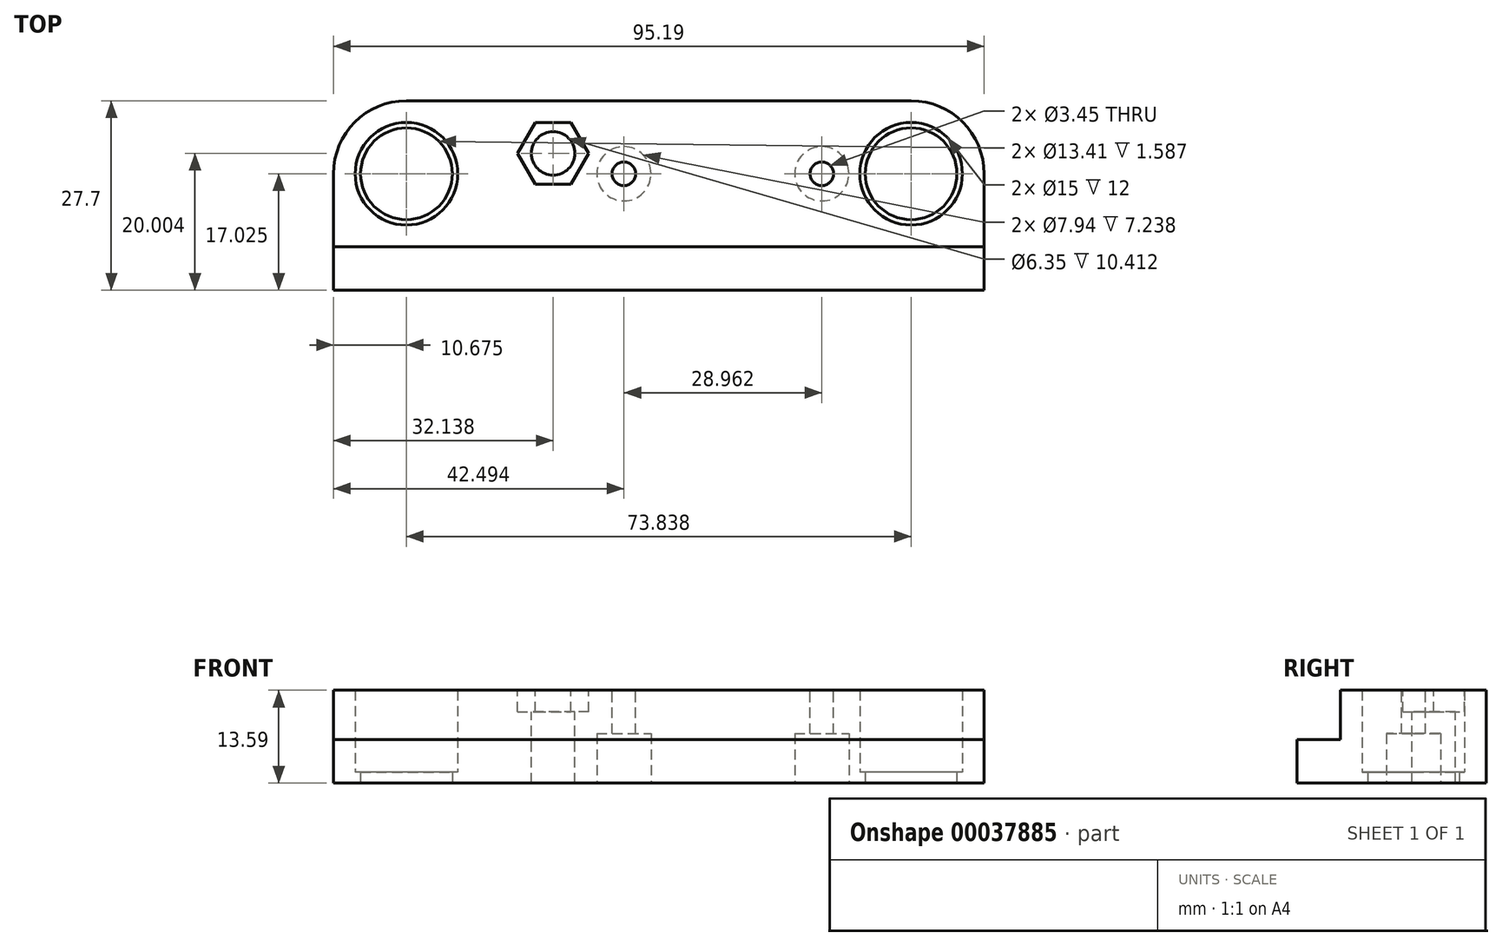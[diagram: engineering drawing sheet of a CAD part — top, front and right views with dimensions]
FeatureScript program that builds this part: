
annotation { "Feature Type Name" : "Feature", "Feature Type Description" : "" }
export const myFeature = defineFeature(function(context is Context, id is Id, definition is map)
    precondition{}
    {
        {
            var Q0;
            Q0=qCreatedBy(makeId("Top.planeOp"),FACE);
            var sketch = newSketch(context, id + "F0", { "sketchPlane" : qUnion([Q0])});
            skLineSegment(sketch, "E0.bottom", {"start": v(0, 0) * mm, "end": v(95.19, 0) * mm});
            skLineSegment(sketch, "E0.top", {"start": v(0, -27.7) * mm, "end": v(95.19, -27.7) * mm});
            skLineSegment(sketch, "E0.left", {"start": v(0, 0) * mm, "end": v(0, -27.7) * mm});
            skLineSegment(sketch, "E0.right", {"start": v(95.19, 0) * mm, "end": v(95.19, -27.7) * mm});
            skLineSegment(sketch, "E1", {"start": v(10.67, 0) * mm, "end": v(10.67, -10.67) * mm, "construction": true});
            skLineSegment(sketch, "E2", {"start": v(10.67, -10.67) * mm, "end": v(0, -10.67) * mm, "construction": true});
            skLineSegment(sketch, "E3", {"start": v(95.19, -10.67) * mm, "end": v(84.51, -10.67) * mm, "construction": true});
            skCircle(sketch, "E4", {"center": v(10.67, -10.67) * mm, "radius": 6.7 * mm});
            skCircle(sketch, "E5", {"center": v(84.51, -10.67) * mm, "radius": 6.7 * mm});
            skSolve(sketch);
        }
        {
            var Q0;
            Q0=qSketchRegion(id+"F0",true);
            extrude(context, id + "F1", {"entities" : qUnion([Q0]), "depth" : 1.59 * mm});
        }
        {
            var Q0;
            Q0=makeQuery(id+"F1.opExtrude","SWEPT_EDGE",EDGE,{"disambiguationData":[OSD([sQuery(id+"F0.wireOp",EDGE,"E0.bottom"),sQuery(id+"F0.wireOp",EDGE,"E0.left")])]});
            var Q1;
            Q1=makeQuery(id+"F1.opExtrude","SWEPT_EDGE",EDGE,{"disambiguationData":[OSD([sQuery(id+"F0.wireOp",EDGE,"E0.bottom"),sQuery(id+"F0.wireOp",EDGE,"E0.right")])]});
            fillet(context, id + "F2", {"entities" : qUnion([Q0, Q1]), "radius" : 10.67 * mm, "tangentPropagation" : true, "allowEdgeOverflow" : false});
        }
        {
            var Q0;
            Q0=makeQuery(id+"F1.opExtrude","CAP_FACE",FACE,{"disambiguationData":[OSD([sQuery(id+"F0.wireOp",EDGE,"E0.bottom"),sQuery(id+"F0.wireOp",EDGE,"E0.top"),sQuery(id+"F0.wireOp",EDGE,"E0.left"),sQuery(id+"F0.wireOp",EDGE,"E0.right"),sQuery(id+"F0.wireOp",EDGE,"E4"),sQuery(id+"F0.wireOp",EDGE,"E5")])],"isStart":false});
            var sketch = newSketch(context, id + "F3", { "sketchPlane" : qUnion([Q0])});
            skLineSegment(sketch, "E6.bottom", {"start": v(0, -10.67) * mm, "end": v(95.19, -10.67) * mm, "construction": true});
            skLineSegment(sketch, "E6.top", {"start": v(0, -21.35) * mm, "end": v(95.19, -21.35) * mm});
            skLineSegment(sketch, "E6.left", {"start": v(0, -10.67) * mm, "end": v(0, -21.35) * mm});
            skLineSegment(sketch, "E6.right", {"start": v(95.19, -10.67) * mm, "end": v(95.19, -21.35) * mm});
            skLineSegment(sketch, "E7", {"start": v(47.6, -21.35) * mm, "end": v(47.6, -27.7) * mm, "construction": true});
            skPoint(sketch, "E7.endSnap0", {"position": v(47.6, -27.7) * mm});
            skCircle(sketch, "E8", {"center": v(10.67, -10.67) * mm, "radius": 7.5 * mm});
            skCircle(sketch, "E9", {"center": v(84.51, -10.67) * mm, "radius": 7.5 * mm});
            skSolve(sketch);
        }
        {
            var Q0;
            Q0=makeQuery(id+"F3.imprint","IMPRINT",FACE,{"disambiguationData":[TD([[makeQuery(id+"F3.imprint","IMPRINT",EDGE,{"derivedFrom":sQuery(id+"F3.wireOp",EDGE,"E6.top")}),1.0]])]});
            extrude(context, id + "F4", {"entities" : qUnion([Q0]), "operationType" : NewBodyOperationType.ADD, "depth" : 12 * mm});
        }
        {
            var Q0;
            {var subQ0=sQuery(id+"F0.wireOp",EDGE,"E0.top");var subQ1=sQuery(id+"F0.wireOp",EDGE,"E0.left");var subQ2=sQuery(id+"F0.wireOp",EDGE,"E0.right");Q0=makeQuery(id+"F4.boolean.opBoolean","SPLIT",FACE,{"disambiguationData":[TD([makeQuery(id+"F1.opExtrude","SWEPT_FACE",FACE,{"disambiguationData":[OSD([subQ0])]})])],"derivedFrom":makeQuery(id+"F1.opExtrude","CAP_FACE",FACE,{"disambiguationData":[OSD([sQuery(id+"F0.wireOp",EDGE,"E0.bottom"),subQ0,subQ1,subQ2,sQuery(id+"F0.wireOp",EDGE,"E4"),sQuery(id+"F0.wireOp",EDGE,"E5")])],"isStart":false})});}
            extrude(context, id + "F5", {"entities" : qUnion([Q0]), "operationType" : NewBodyOperationType.ADD, "depth" : 4.76 * mm});
        }
        {
            var Q0;
            Q0=makeQuery(id+"F4.opExtrude","CAP_FACE",FACE,{"disambiguationData":[OSD([sQuery(id+"F0.wireOp",EDGE,"E0.bottom"),sQuery(id+"F0.wireOp",EDGE,"E0.top"),sQuery(id+"F0.wireOp",EDGE,"E0.left"),sQuery(id+"F0.wireOp",EDGE,"E0.right"),sQuery(id+"F0.wireOp",EDGE,"E4"),sQuery(id+"F0.wireOp",EDGE,"E5"),sQuery(id+"F3.wireOp",EDGE,"E6.top"),sQuery(id+"F3.wireOp",EDGE,"E6.left"),sQuery(id+"F3.wireOp",EDGE,"E6.right"),sQuery(id+"F3.wireOp",EDGE,"E8"),sQuery(id+"F3.wireOp",EDGE,"E9")])],"isStart":false});
            var sketch = newSketch(context, id + "F6", { "sketchPlane" : qUnion([Q0])});
            skCircle(sketch, "E10", {"center": v(42.5, -10.67) * mm, "radius": 5.56 * mm, "construction": true});
            skPoint(sketch, "E11", {"position": v(47.6, -10.67) * mm});
            skCircle(sketch, "E12", {"center": v(42.5, -10.67) * mm, "radius": 1.73 * mm});
            skCircle(sketch, "E13", {"center": v(71.46, -10.67) * mm, "radius": 1.73 * mm});
            skLineSegment(sketch, "E14", {"start": v(47.6, -10.67) * mm, "end": v(47.6, -21.35) * mm, "construction": true});
            skCircle(sketch, "E15", {"center": v(32.14, -7.7) * mm, "radius": 3.18 * mm});
            skLineSegment(sketch, "E16", {"start": v(10.67, -10.67) * mm, "end": v(10.67, -7.7) * mm, "construction": true});
            skLineSegment(sketch, "E17", {"start": v(10.67, -7.7) * mm, "end": v(32.14, -7.7) * mm, "construction": true});
            skLineSegment(sketch, "E18", {"start": v(47.6, -10.67) * mm, "end": v(71.46, -10.67) * mm, "construction": true});
            skLineSegment(sketch, "E19", {"start": v(47.6, -10.67) * mm, "end": v(42.5, -10.67) * mm, "construction": true});
            skCircle(sketch, "E20", {"center": v(32.14, -7.7) * mm, "radius": 5.22 * mm, "construction": true});
            skCircle(sketch, "E21", {"center": v(71.46, -10.67) * mm, "radius": 5.56 * mm, "construction": true});
            skSolve(sketch);
        }
        {
            var Q0;
            Q0=qSketchRegion(id+"F6",true);
            var Q1;
            Q1=makeQuery(id+"F1.opExtrude","CAP_FACE",FACE,{"disambiguationData":[OSD([sQuery(id+"F0.wireOp",EDGE,"E0.bottom"),sQuery(id+"F0.wireOp",EDGE,"E0.top"),sQuery(id+"F0.wireOp",EDGE,"E0.left"),sQuery(id+"F0.wireOp",EDGE,"E0.right"),sQuery(id+"F0.wireOp",EDGE,"E4"),sQuery(id+"F0.wireOp",EDGE,"E5")])],"isStart":true});
            extrude(context, id + "F7", {"entities" : qUnion([Q0]), "operationType" : NewBodyOperationType.REMOVE, "endBound" : BoundingType.UP_TO_SURFACE, "oppositeDirection" : true, "endBoundEntityFace" : qUnion([Q1]), "depth" : 25.4 * mm});
        }
        {
            var Q0;
            Q0=makeQuery(id+"F1.opExtrude","CAP_FACE",FACE,{"disambiguationData":[OSD([sQuery(id+"F0.wireOp",EDGE,"E0.bottom"),sQuery(id+"F0.wireOp",EDGE,"E0.top"),sQuery(id+"F0.wireOp",EDGE,"E0.left"),sQuery(id+"F0.wireOp",EDGE,"E0.right"),sQuery(id+"F0.wireOp",EDGE,"E4"),sQuery(id+"F0.wireOp",EDGE,"E5")])],"isStart":true});
            var sketch = newSketch(context, id + "F8", { "sketchPlane" : qUnion([Q0])});
            skCircle(sketch, "E22", {"center": v(71.46, 10.67) * mm, "radius": 3.97 * mm});
            skCircle(sketch, "E23", {"center": v(42.5, 10.67) * mm, "radius": 3.97 * mm});
            skSolve(sketch);
        }
        {
            var Q0;
            Q0=qSketchRegion(id+"F8",true);
            extrude(context, id + "F9", {"entities" : qUnion([Q0]), "operationType" : NewBodyOperationType.REMOVE, "oppositeDirection" : true, "depth" : 7.24 * mm});
        }
        {
            var Q0;
            Q0=makeQuery(id+"F4.opExtrude","CAP_FACE",FACE,{"disambiguationData":[OSD([sQuery(id+"F0.wireOp",EDGE,"E0.bottom"),sQuery(id+"F0.wireOp",EDGE,"E0.top"),sQuery(id+"F0.wireOp",EDGE,"E0.left"),sQuery(id+"F0.wireOp",EDGE,"E0.right"),sQuery(id+"F0.wireOp",EDGE,"E4"),sQuery(id+"F0.wireOp",EDGE,"E5"),sQuery(id+"F3.wireOp",EDGE,"E6.top"),sQuery(id+"F3.wireOp",EDGE,"E6.left"),sQuery(id+"F3.wireOp",EDGE,"E6.right"),sQuery(id+"F3.wireOp",EDGE,"E8"),sQuery(id+"F3.wireOp",EDGE,"E9")])],"isStart":false});
            var sketch = newSketch(context, id + "F10", { "sketchPlane" : qUnion([Q0])});
            skCircle(sketch, "E24.cCircle", {"center": v(32.14, -7.7) * mm, "radius": 4.52 * mm, "construction": true});
            skLineSegment(sketch, "E24.0", {"start": v(29.53, -3.18) * mm, "end": v(34.75, -3.18) * mm});
            skLineSegment(sketch, "E24.1", {"start": v(34.75, -3.18) * mm, "end": v(37.36, -7.7) * mm});
            skLineSegment(sketch, "E24.2", {"start": v(37.36, -7.7) * mm, "end": v(34.75, -12.22) * mm});
            skLineSegment(sketch, "E24.3", {"start": v(34.75, -12.22) * mm, "end": v(29.53, -12.22) * mm});
            skLineSegment(sketch, "E24.4", {"start": v(29.53, -12.22) * mm, "end": v(26.92, -7.7) * mm});
            skLineSegment(sketch, "E24.5", {"start": v(26.92, -7.7) * mm, "end": v(29.53, -3.18) * mm});
            skPoint(sketch, "E24.0.midPoint", {"position": v(32.14, -3.18) * mm});
            skSolve(sketch);
        }
        {
            var Q0;
            Q0=qSketchRegion(id+"F10",true);
            extrude(context, id + "F11", {"entities" : qUnion([Q0]), "operationType" : NewBodyOperationType.REMOVE, "oppositeDirection" : true, "depth" : 3.17 * mm});
        }
    });
